FREECAD ASSEMBLY — COMPONENT RECIPES ("portal-stepper-assembly")

This assembly document has 3 components, labeled P0..P2 below (a component is one placed body or linked part). 3 of them carry a construction recipe — the FreeCAD feature program that regenerates the part from scratch, quoted from this document or its linked companion documents; the rest are supplied as boundary geometry only. No exploded tour is included for this assembly.
COMPONENT P0 — recipe-attached ("Coupler 6.35-8mm Without Screw001", a linked part whose construction recipe lives in a companion FreeCAD document of the same project; that document's serialized recipe follows).
Construction recipe (the companion document, serialized — sketch geometry with constraints, then the solid features built on it; lengths are millimeters unless a unit is written):

FCSTD DOCUMENT  (FreeCAD 1.0R39319 (Git))
Label: stepper-assembly
License: All rights reserved
LicenseURL: http://en.wikipedia.org/wiki/All_rights_reserved
objects: Part::Feature×18, App::FeaturePython×16, App::Part×7, App::Link×4, Part::FeaturePython×1, Assembly::JointGroup×1, Assembly::AssemblyObject×1
note: 19 computed .brp shape members not serialized (recipe doc carries the construction recipe); baked Part::Feature solids carry a one-line shape summary decoded from their .brp
EXTERNAL_REF file=../parts/NEMA23-holder.FCStd obj=Part
EXTERNAL_REF file=../parts/x-profile.FCStd obj=Part

FEATURE [App::Link] nema23_holder  label="nema23-holder"
  LinkPlacement = pos=(0,0,0) rot=(-0.953069,0,-0.302943;2e-06rad)
  LinkedObject = -> <external ../parts/NEMA23-holder.FCStd>#Part
  Placement = pos=(0,0,0) rot=(-0.953069,0,-0.302943;2e-06rad)
FEATURE [Part::Feature] Part__Feature  label="Coupler 6.35-8mm Without Screw"
  shape: bbox 20.93 x 20.57 x 29.69 mm, 170 faces (baked)
FEATURE [App::Part] Coupler_6_35_8mm_Without_Screw  label="Coupler 6.35-8mm Without Screw001"
  Group = -> [Part__Feature]
  Origin = -> Origin001
  Placement = pos=(32.5,96.0278,35.5) rot=(0.993786,0.078707,-0.078701;1.57705rad)
FEATURE [Part::Feature] Part__Feature001  label="Power Step - PSM57HS2A54-2P"
  shape: bbox 56.89 x 76.8 x 56.89 mm, 96 faces (baked)
FEATURE [Part::Feature] Part__Feature002  label="Power Step - PSM57HS2A54-2P001"
  shape: bbox 56.6 x 33 x 56.6 mm, 50 faces (baked)
FEATURE [App::Part] Power_Step___PSM57HS2A54_2P  label="Power Step - PSM57HS2A54-2P002"
  Group = -> [Part__Feature001,Part__Feature002]
  Origin = -> Origin002
  Placement = pos=(32.5,44.5,35.5) rot=(-2e-06,1,-4e-06;1.5708rad)
FEATURE [Part::Feature] Part__Feature003  label="SC8UU"
  shape: bbox 34 x 22 x 30 mm, 48 faces (baked)
FEATURE [App::Part] Part  label="bearing-support"
  Group = -> [Part__Feature003]
  Origin = -> Origin003
  Placement = pos=(32.498,479.614,35.5061) rot=(-1,-3e-06,3e-06;1.57078rad)
FEATURE [App::FeaturePython] Joint  label="Cylindrical"  # Assembly joint (typed FeaturePython)
  Activated = true
  AngleMax = 0
  AngleMin = 0
  Detach1 = false
  Detach2 = false
  Distance = 0
  Distance2 = 0
  EnableAngleMax = false
  EnableAngleMin = false
  EnableLengthMax = false
  EnableLengthMin = false
  JointType = 2 (Cylindrical)
  LengthMax = 0
  LengthMin = 0
  Placement1 = pos=(0,29.5,0) rot=(0.57735,0.57735,0.57735;4.18879rad)
  Placement2 = pos=(32.5,-1.42e-14,35.5) rot=(1,0,0;1.5708rad)
  Reference1 = -> Assembly [Power_Step___PSM57HS2A54_2P.Part__Feature001.Edge20,Power_Step___PSM57HS2A54_2P.Part__Feature001.Edge20]
  Reference2 = -> Assembly [nema23_holder.Body001.Edge20,nema23_holder.Body001.Edge20]
FEATURE [Part::FeaturePython] ThreadedRod  label="M8x400-ThreadedRod"  # WARN: FeaturePython — macro-defined, semantics opaque (R4)
  Diameter = 9
  DiameterCustom = 8
  Invert = false
  LeftHanded = false
  Length = 400
  MatchOuter = false
  OffsetAngle = 0
  PitchCustom = 1
  Placement = pos=(32.5,94.614,35.5) rot=(-0.04014,0.706542,-0.706531;3.22182rad)
  Thread = false
  Type = 4
FEATURE [App::FeaturePython] GroundedJoint  # Assembly grounded joint (typed FeaturePython)
  ObjectToGround = -> nema23_holder
  Placement = pos=(0,0,0) rot=(-0.953069,0,-0.302943;2e-06rad)
FEATURE [App::FeaturePython] GroundedJoint001  # Assembly grounded joint (typed FeaturePython)
  ObjectToGround = -> Power_Step___PSM57HS2A54_2P
  Placement = pos=(32.5,44.5,35.5) rot=(-2e-06,1,-4e-06;1.5708rad)
FEATURE [App::FeaturePython] Joint001  label="Cylindrical001"  # Assembly joint (typed FeaturePython)
  Activated = true
  AngleMax = 0
  AngleMin = 0
  Detach1 = false
  Detach2 = false
  Distance = 0
  Distance2 = 0
  EnableAngleMax = false
  EnableAngleMin = false
  EnableLengthMax = false
  EnableLengthMin = false
  JointType = 2 (Cylindrical)
  LengthMax = 0
  LengthMin = 0
  Placement1 = pos=(-3.6e-15,7.1e-15,-1.25) rot=(0,0,1;0rad)
  Placement2 = pos=(0,37.9092,0) rot=(-0.57735,-0.57735,0.57735;4.18879rad)
  Reference1 = -> Assembly [ThreadedRod.Face3,ThreadedRod.Edge1]
  Reference2 = -> Assembly [Power_Step___PSM57HS2A54_2P.Part__Feature001.Face80,Power_Step___PSM57HS2A54_2P.Part__Feature001.Face80]
FEATURE [App::FeaturePython] Joint002  label="Cylindrical002"  # Assembly joint (typed FeaturePython)
  Activated = true
  AngleMax = 0
  AngleMin = 0
  Detach1 = false
  Detach2 = false
  Distance = 0
  Distance2 = 0
  EnableAngleMax = false
  EnableAngleMin = false
  EnableLengthMax = false
  EnableLengthMin = false
  JointType = 2 (Cylindrical)
  LengthMax = 0
  LengthMin = 0
  Placement1 = pos=(0,0,-8) rot=(0,1,0;3.14159rad)
  Placement2 = pos=(-3.6e-15,7.1e-15,-1.25) rot=(0,0,1;0rad)
  Reference1 = -> Assembly [Coupler_6_35_8mm_Without_Screw.Part__Feature.Face28,Coupler_6_35_8mm_Without_Screw.Part__Feature.Edge12]
  Reference2 = -> Assembly [ThreadedRod.Face3,ThreadedRod.Edge1]
FEATURE [App::FeaturePython] GroundedJoint002  # Assembly grounded joint (typed FeaturePython)
  ObjectToGround = -> Coupler_6_35_8mm_Without_Screw
  Placement = pos=(32.5,96.0278,35.5) rot=(0.993786,0.078707,-0.078701;1.57705rad)
FEATURE [App::FeaturePython] GroundedJoint003  # Assembly grounded joint (typed FeaturePython)
  ObjectToGround = -> ThreadedRod
  Placement = pos=(32.5,94.614,35.5) rot=(-0.04014,0.706542,-0.706531;3.22182rad)
FEATURE [App::FeaturePython] Joint003  label="Cylindrical003"  # Assembly joint (typed FeaturePython)
  Activated = true
  AngleMax = 0
  AngleMin = 0
  Detach1 = false
  Detach2 = false
  Distance = 0
  Distance2 = 0
  EnableAngleMax = false
  EnableAngleMin = false
  EnableLengthMax = false
  EnableLengthMin = false
  JointType = 2 (Cylindrical)
  LengthMax = 0
  LengthMin = 0
  Placement1 = pos=(0,0,-14) rot=(0,1,0;3.14159rad)
  Placement2 = pos=(-1.847e-13,-5.68e-14,-398.75) rot=(0,0,1;0rad)
  Reference1 = -> Assembly [Part.Part__Feature003.Face38,Part.Part__Feature003.Edge1]
  Reference2 = -> Assembly [ThreadedRod.Face3,ThreadedRod.Edge2]
FEATURE [App::Link] x_profile  label="x-profile"
  LinkPlacement = pos=(-167.5,276.601,55.7999) rot=(-0.577347,0.577348,0.577356;2.09438rad)
  LinkedObject = -> <external ../parts/x-profile.FCStd>#Part
  Placement = pos=(-167.5,276.601,55.7999) rot=(-0.577347,0.577348,0.577356;2.09438rad)
FEATURE [Part::Feature] Part__Feature004  label="Anti-Backlash_Nut_TR8x2"
  shape: bbox 13.31 x 19.2 x 12.91 mm, 12 faces (baked)
FEATURE [Part::Feature] Part__Feature005  label="Anti-Backlash_Nut_TR8x003"
  shape: bbox 22 x 16.19 x 22 mm, 78 faces (baked)
FEATURE [Part::Feature] Part__Feature006  label="Anti-Backlash_Nut_TR8x004"
  shape: bbox 14 x 15.64 x 14 mm, 59 faces (baked)
FEATURE [App::Part] Anti_Backlash_Nut_TR8x2  label="Anti-Backlash_Nut_TR8x005"
  Group = -> [Part__Feature004,Part__Feature005,Part__Feature006]
  Origin = -> Origin004
  Placement = pos=(32.5,316.91,35.5) rot=(0,1,0;0rad)
FEATURE [Part::Feature] Part__Feature007  label="Round Flange Trapezoidal Tr8"
  shape: bbox 22 x 22 x 15 mm, 21 faces (baked)
FEATURE [App::Part] Part001  label="Nut-TR8"
  Group = -> [Part__Feature007]
  Origin = -> Origin005
  Placement = pos=(32.4991,261.601,35.5026) rot=(-0.577351,0.577355,-0.577345;4.18878rad)
FEATURE [App::FeaturePython] GroundedJoint005  # Assembly grounded joint (typed FeaturePython)
  ObjectToGround = -> Part001
  Placement = pos=(32.4991,261.601,35.5026) rot=(-0.577351,0.577355,-0.577345;4.18878rad)
FEATURE [App::FeaturePython] GroundedJoint006  # Assembly grounded joint (typed FeaturePython)
  ObjectToGround = -> Anti_Backlash_Nut_TR8x2
  Placement = pos=(32.5,316.91,35.5) rot=(0,1,0;0rad)
FEATURE [Part::Feature] Part__Feature008  label="MGN9-H"
  shape: bbox 20 x 8 x 29.9 mm, 47 faces (baked)
FEATURE [Part::Feature] Part__Feature009  label="MGN9-H001"
  shape: bbox 20 x 7.7 x 4.1 mm, 23 faces (baked)
FEATURE [Part::Feature] Part__Feature010  label="MGN9-H002"
  shape: bbox 2.603 x 2.603 x 1.283 mm, 15 faces (baked)
FEATURE [Part::Feature] Part__Feature011  label="MGN9-H003"
  shape: bbox 2.603 x 2.603 x 1.283 mm, 15 faces (baked)
FEATURE [Part::Feature] Part__Feature012  label="MGN9-H004"
  shape: bbox 20 x 7.7 x 0.9 mm, 57 faces (baked)
FEATURE [Part::Feature] Part__Feature013  label="MGN9-H005"
  shape: bbox 20 x 7.7 x 4.1 mm, 23 faces (baked)
FEATURE [Part::Feature] Part__Feature014  label="MGN9-H006"
  shape: bbox 20 x 7.7 x 0.9 mm, 57 faces (baked)
FEATURE [Part::Feature] Part__Feature015  label="MGN9-H007"
  shape: bbox 2.603 x 2.603 x 1.283 mm, 15 faces (baked)
FEATURE [Part::Feature] Part__Feature016  label="MGN9-H008"
  shape: bbox 2.603 x 2.603 x 1.283 mm, 15 faces (baked)
FEATURE [App::Part] MGN9_H  label="block-MGN9-H009"
  Group = -> [Part__Feature008,Part__Feature009,Part__Feature010,Part__Feature011,Part__Feature012,Part__Feature013,Part__Feature014,Part__Feature015,Part__Feature016]
  Origin = -> Origin006
  Placement = pos=(-149.71,296.602,11.8002) rot=(1e-06,0.781989,0.782002;3.14159rad)
FEATURE [App::Link] block_MGN9_H009  label="block-MGN9-H010"
  LinkPlacement = pos=(214.983,296.784,11.8004) rot=(1,-1e-06,-1e-06;1.57081rad)
  LinkedObject = -> MGN9_H
  Placement = pos=(214.983,296.784,11.8004) rot=(1,-1e-06,-1e-06;1.57081rad)
FEATURE [App::Link] rail  label="rail001"
  LinkPlacement = pos=(214.965,441.284,9.01518) rot=(1,-1e-06,-1e-06;1.57081rad)
  LinkedObject = -> Part002
  Placement = pos=(214.965,441.284,9.01518) rot=(1,-1e-06,-1e-06;1.57081rad)
FEATURE [App::FeaturePython] GroundedJoint007  # Assembly grounded joint (typed FeaturePython)
  ObjectToGround = -> x_profile
  Placement = pos=(-167.5,276.601,55.7999) rot=(-0.577347,0.577348,0.577356;2.09438rad)
FEATURE [Part::Feature] Part__Feature017  label="MGN9"
  shape: bbox 9 x 6.5 x 250 mm, 130 faces (baked)
FEATURE [App::Part] Part002  label="rail"
  Group = -> [Part__Feature017]
  Origin = -> Origin007
  Placement = pos=(-149.691,441.102,8.99001) rot=(1,-1e-06,-1e-06;1.57081rad)
FEATURE [App::FeaturePython] Joint015  label="Distance005"  # Assembly joint (typed FeaturePython)
  Activated = true
  AngleMax = 0
  AngleMin = 0
  Detach1 = false
  Detach2 = false
  Distance = 0
  Distance2 = 0
  EnableAngleMax = false
  EnableAngleMin = false
  EnableLengthMax = false
  EnableLengthMin = false
  JointType = 5 (Distance)
  LengthMax = 0
  LengthMin = 0
  Placement1 = pos=(3.13175,-1.3,19.5) rot=(0,-1,0;1.5708rad)
  Placement2 = pos=(-3.15008,1.5125,125) rot=(0,1,0;1.5708rad)
  Reference1 = -> Assembly [MGN9_H.Part__Feature012.Face15,MGN9_H.Part__Feature012.Face15]
  Reference2 = -> Assembly [Part002.Part__Feature017.Face63,Part002.Part__Feature017.Vertex149]
FEATURE [App::FeaturePython] Joint016  label="Distance006"  # Assembly joint (typed FeaturePython)
  Activated = true
  AngleMax = 0
  AngleMin = 0
  Detach1 = false
  Detach2 = false
  Distance = 0
  Distance2 = 0
  EnableAngleMax = false
  EnableAngleMin = false
  EnableLengthMax = false
  EnableLengthMin = false
  JointType = 5 (Distance)
  LengthMax = 0
  LengthMin = 0
  Placement1 = pos=(3.13175,-1.3,-19.5) rot=(-0.707107,0,0.707107;3.14159rad)
  Placement2 = pos=(3.15008,1.5125,125) rot=(0,-1,0;1.5708rad)
  Reference1 = -> Assembly [block_MGN9_H009.Part__Feature014.Face15,block_MGN9_H009.Part__Feature014.Face15]
  Reference2 = -> Assembly [rail.Part__Feature017.Face73,rail.Part__Feature017.Vertex169]
FEATURE [App::FeaturePython] GroundedJoint008  # Assembly grounded joint (typed FeaturePython)
  ObjectToGround = -> Part002
  Placement = pos=(-149.691,441.102,8.99001) rot=(1,-1e-06,-1e-06;1.57081rad)
FEATURE [App::FeaturePython] GroundedJoint009  # Assembly grounded joint (typed FeaturePython)
  ObjectToGround = -> MGN9_H
  Placement = pos=(-149.71,296.602,11.8002) rot=(1e-06,0.781989,0.782002;3.14159rad)
FEATURE [App::FeaturePython] GroundedJoint010  # Assembly grounded joint (typed FeaturePython)
  ObjectToGround = -> Part
  Placement = pos=(32.498,479.614,35.5061) rot=(-1,-3e-06,3e-06;1.57078rad)
FEATURE [Assembly::JointGroup] Joints
  Group = -> [Joint,GroundedJoint,GroundedJoint001,Joint001,Joint002,GroundedJoint002,GroundedJoint003,Joint003,GroundedJoint005,GroundedJoint006,GroundedJoint007,Joint015,Joint016,GroundedJoint008,GroundedJoint009,GroundedJoint010]
FEATURE [Assembly::AssemblyObject] Assembly  label="stepper-assembly"
  Group = -> [Joints,nema23_holder,Power_Step___PSM57HS2A54_2P,Coupler_6_35_8mm_Without_Screw,Part,Joint,ThreadedRod,GroundedJoint,GroundedJoint001,Joint001,Joint002,GroundedJoint002,GroundedJoint003,Joint003,x_profile,Anti_Backlash_Nut_TR8x2,Part001,GroundedJoint005,GroundedJoint006,block_MGN9_H009,rail,MGN9_H,Part002,GroundedJoint007,Joint015,Joint016,GroundedJoint008,GroundedJoint009,GroundedJoint010]
  Origin = -> Origin
  Type = Assembly
COMPONENT P1 — same part as P0; its construction recipe is shown at P0.
COMPONENT P2 — same part as P0; its construction recipe is shown at P0.
PROVENANCE & LICENSES
A FreeCAD (.FCStd) document from a public repository crawl; recipes are the document's own serialized feature recipes (and, for linked parts, companion documents' recipes).
License: as declared in the source repository (recorded in the dataset sidecar).
